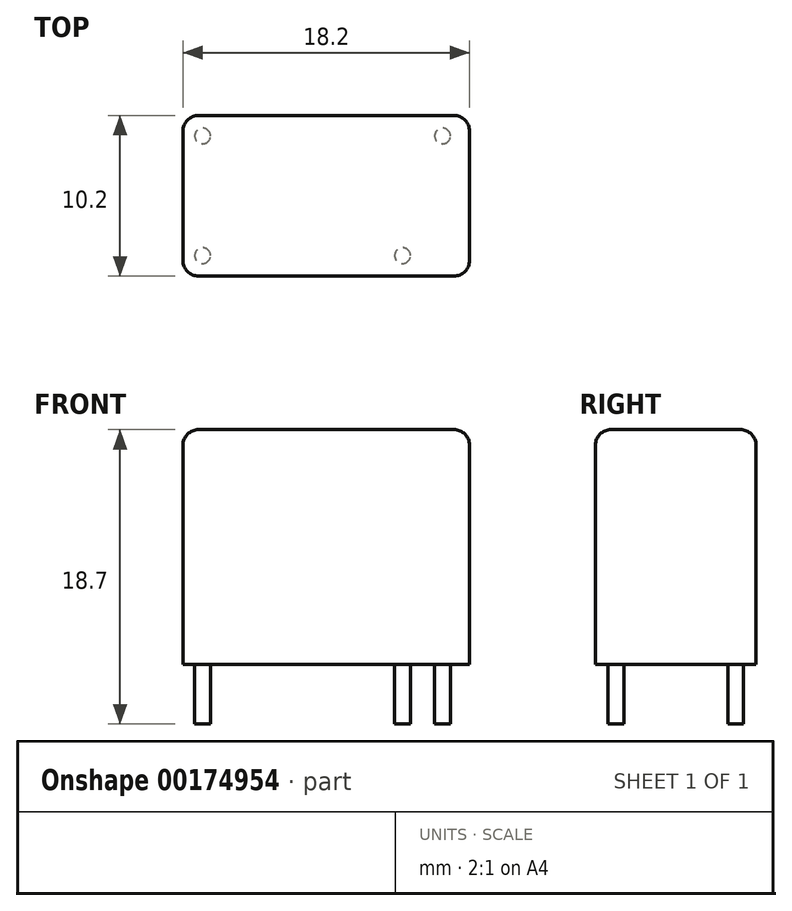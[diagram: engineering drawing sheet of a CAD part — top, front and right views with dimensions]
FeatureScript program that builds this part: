
annotation { "Feature Type Name" : "Feature", "Feature Type Description" : "" }
export const myFeature = defineFeature(function(context is Context, id is Id, definition is map)
    precondition{}
    {
        {
            var Q0;
            Q0=qCreatedBy(makeId("Top.planeOp"),FACE);
            var sketch = newSketch(context, id + "F0", { "sketchPlane" : qUnion([Q0])});
            skLineSegment(sketch, "E0.bottom", {"start": v(-9.1, 5.1) * mm, "end": v(9.1, 5.1) * mm});
            skLineSegment(sketch, "E0.top", {"start": v(-9.1, -5.1) * mm, "end": v(9.1, -5.1) * mm});
            skLineSegment(sketch, "E0.left", {"start": v(-9.1, 5.1) * mm, "end": v(-9.1, -5.1) * mm});
            skLineSegment(sketch, "E0.right", {"start": v(9.1, 5.1) * mm, "end": v(9.1, -5.1) * mm});
            skSolve(sketch);
        }
        {
            var Q0;
            Q0 = qSketchRegion(id + "F0", true);
            extrude(context, id + "F1", {"entities" : qUnion([Q0]), "depth" : 14.9 * mm});
        }
        {
            var Q0;
            Q0=makeQuery(id+"F1.opExtrude","CAP_EDGE",EDGE,{"disambiguationData":[OSD([sQuery(id+"F0.wireOp",EDGE,"E0.top")])],"isStart":false});
            var Q1;
            Q1=makeQuery(id+"F1.opExtrude","CAP_EDGE",EDGE,{"disambiguationData":[OSD([sQuery(id+"F0.wireOp",EDGE,"E0.right")])],"isStart":false});
            var Q2;
            Q2=makeQuery(id+"F1.opExtrude","CAP_EDGE",EDGE,{"disambiguationData":[OSD([sQuery(id+"F0.wireOp",EDGE,"E0.bottom")])],"isStart":false});
            var Q3;
            Q3=makeQuery(id+"F1.opExtrude","CAP_EDGE",EDGE,{"disambiguationData":[OSD([sQuery(id+"F0.wireOp",EDGE,"E0.left")])],"isStart":false});
            var Q4;
            Q4=makeQuery(id+"F1.opExtrude","SWEPT_EDGE",EDGE,{"disambiguationData":[OSD([sQuery(id+"F0.wireOp",EDGE,"E0.top"),sQuery(id+"F0.wireOp",EDGE,"E0.right")])]});
            var Q5;
            Q5=makeQuery(id+"F1.opExtrude","SWEPT_EDGE",EDGE,{"disambiguationData":[OSD([sQuery(id+"F0.wireOp",EDGE,"E0.bottom"),sQuery(id+"F0.wireOp",EDGE,"E0.right")])]});
            var Q6;
            Q6=makeQuery(id+"F1.opExtrude","SWEPT_EDGE",EDGE,{"disambiguationData":[OSD([sQuery(id+"F0.wireOp",EDGE,"E0.top"),sQuery(id+"F0.wireOp",EDGE,"E0.left")])]});
            var Q7;
            Q7=makeQuery(id+"F1.opExtrude","SWEPT_EDGE",EDGE,{"disambiguationData":[OSD([sQuery(id+"F0.wireOp",EDGE,"E0.bottom"),sQuery(id+"F0.wireOp",EDGE,"E0.left")])]});
            fillet(context, id + "F2", {"entities" : qUnion([Q0, Q1, Q2, Q3, Q4, Q5, Q6, Q7]), "radius" : 1 * mm, "tangentPropagation" : true, "allowEdgeOverflow" : false});
        }
        {
            var Q0;
            Q0=makeQuery(id+"F1.opExtrude","CAP_FACE",FACE,{"disambiguationData":[OSD([sQuery(id+"F0.wireOp",EDGE,"E0.bottom"),sQuery(id+"F0.wireOp",EDGE,"E0.top"),sQuery(id+"F0.wireOp",EDGE,"E0.left"),sQuery(id+"F0.wireOp",EDGE,"E0.right")])],"isStart":true});
            var sketch = newSketch(context, id + "F3", { "sketchPlane" : qUnion([Q0])});
            skCircle(sketch, "E1", {"center": v(-7.85, 3.8) * mm, "radius": 0.5 * mm});
            skCircle(sketch, "E2.MirrorC", {"center": v(-7.85, -3.8) * mm, "radius": 0.5 * mm});
            skCircle(sketch, "E3", {"center": v(4.85, 3.8) * mm, "radius": 0.5 * mm});
            skCircle(sketch, "E4", {"center": v(7.4, -3.8) * mm, "radius": 0.5 * mm});
            skSolve(sketch);
        }
        {
            var Q0;
            Q0 = qSketchRegion(id + "F3", true);
            extrude(context, id + "F4", {"entities" : qUnion([Q0]), "depth" : 3.8 * mm});
        }
    });
